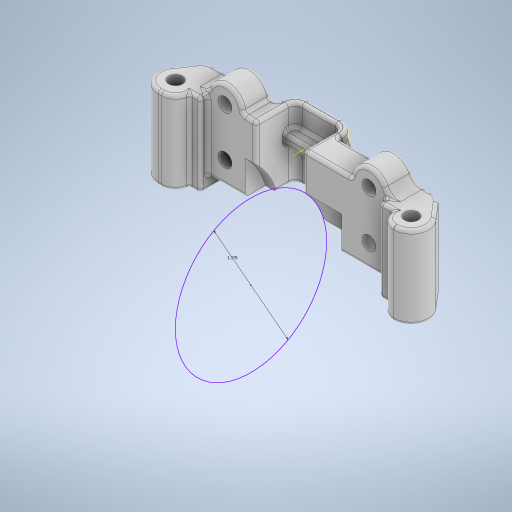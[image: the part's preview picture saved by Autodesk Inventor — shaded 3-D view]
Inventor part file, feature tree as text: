
AUTODESK INVENTOR PART (.ipt)
format: ipt  version: 2024 (Build 280153000, 153)  size: 1,028,608 bytes
history: native  units: in
note: dims shown in document units (in); Inventor stores cm internally (conversion verified against a paired STEP export)
features: fillet x17, sketch x16, extrude x13, pattern_linear x2, hole x2, projected_geometry x2, plane x1, rib x1
ambient origin geometry x8: Origin, YZ Plane, XZ Plane, XY Plane, X Axis, Y Axis, Z Axis, Center Point
bodies: Solid1 (feature_tree)
feature tree (54):
  extrude  "Extrusion1"  Depth=0.415in
  extrude  "Extrusion2"  Depth=1.62in
  fillet  "Fillet1"  Radius=0.315in
  extrude  "Extrusion3"  Depth=0.125in TaperAngle=0.0deg
  extrude  "Extrusion4"  TaperAngle=0.0deg  [1 undecoded]
  extrude  "Extrusion5"  Depth=0.25in TaperAngle=0.0deg
  fillet  "Fillet2"  Radius=0.315in
  extrude  "Extrusion6"  Depth=0.25in TaperAngle=0.0deg
  extrude  "Extrusion7"  Depth=0.55in
  pattern_linear  "Rectangular Pattern1"  Count1=2 Spacing1=0.415in
  extrude  "Extrusion8"  Depth=0.01in TaperAngle=0.0deg
  extrude  "Extrusion9"  Depth=0.032in
  fillet  "Fillet3"  Radius=0.032in
  fillet  "Fillet4"  Radius=0.23in
  fillet  "Fillet5"  Radius=0.23in
  extrude  "Extrusion10"  Depth=0.032in TaperAngle=0.0deg
  fillet  "Fillet6"  Radius=0.032in
  fillet  "Fillet7"  Radius=0.032in
  fillet  "Fillet8"  Radius=0.032in
  fillet  "Fillet9"  Radius=0.125in
  fillet  "Fillet10"  Radius=0.032in
  fillet  "Fillet11"  Radius=0.03in
  fillet  "Fillet12"  Radius=0.03in
  fillet  "Fillet13"  Radius=0.031in
  fillet  "Fillet14"  Radius=0.031in
  fillet  "Fillet15"  Radius=0.031in
  plane  "Work Plane1"
  rib  "Rib1"
  fillet  "Fillet16"  [1 undecoded]
  pattern_linear  "Rectangular Pattern2"  Spacing1=0.115in  [1 undecoded]
  extrude  "Extrusion11"  Depth=0.032in
  fillet  "Fillet17"  Radius=0.031in
  hole  "Hole1"  [1 undecoded]
  hole  "Hole2"  [1 undecoded]
  extrude  "Extrusion12"  Depth=0.032in
  extrude  "Extrusion13"  Depth=0.032in
  sketch  "Sketch1"  dims[d0=0.75in d1=0.415in]
  sketch  "Sketch3"  dims[d2=0.8272in d3=1.62in d4=0.315in d5=0.0in]
  sketch  "Sketch4"  dims[d6=0.315in d7=0.125in d8=0.0in]
  sketch  "Sketch5"  dims[d9=0.1575in d10=0.0in d11=0.0in]
  sketch  "Sketch6"  dims[d12=0.6375in d13=0.25in d14=0.0in d15=0.315in]
  sketch  "Sketch7"  dims[d16=0.315in d17=0.25in d18=0.0in]
  sketch  "Sketch8"  dims[d19=0.125in d20=0.55in]
  sketch  "Sketch9"  dims[d21=0.415in]
  sketch  "Sketch10"  dims[d22=0.125in]
  sketch  "Sketch11"  dims[d23=0.0625in]
  sketch  "Sketch12"  dims[d24=0.25in d25=0.0in]
  sketch  "Sketch13"  dims[d26=0.4281in]
  sketch  "Sketch14"  dims[d27=0.4281in]
  sketch  "Sketch15"  dims[d28=0.1in d29=0.0in d30=0.7874in d32=0.415in]
  sketch  "Sketch16"  dims[d34=0.0in d35=0.0in d36=0.01in d37=0.0in]
  sketch  "Sketch17"  dims[d38=0.125in d39=0.015in d40=0.032in d41=0.23in d42=0.23in d43=0.15in d44=0.0in d45=0.032in d46=0.032in d47=0.032in d48=0.125in d49=0.032in d50=0.03in d51=0.03in d52=0.031in d53=0.031in d54=0.031in d55=-0.25in d56=0.115in d57=0.1in d58=0.1in d59=0.0in d60=0.0in d61=0.1in d62=0.1in d63=0.031in d64=0.7874in d66=0.435in d67=0.0in d68=0.0in d69=0.015in d70=0.125in d71=0.75in d72=0.119in d73=0.25in d74=0.5635in d75=1.0in d76=0.8108in d77=0.125in d78=0.75in d79=0.375in d80=0.25in d81=0.5635in d82=1.0in d83=0.8108in d84=1.37in d85=0.35in d86=0.0in d87=0.1in d88=0.0in d89=0.0in d90=0.0in d91=0.0in d92=0.0in]
  projected_geometry  "Project Cut Edges1"
  projected_geometry  "Project Cut Edges2"
note: 5 required parameter values undecoded (feature->parameter linkage not recoverable at this tier; creation-order binding heuristic only, values carry confidence <= 0.55)
